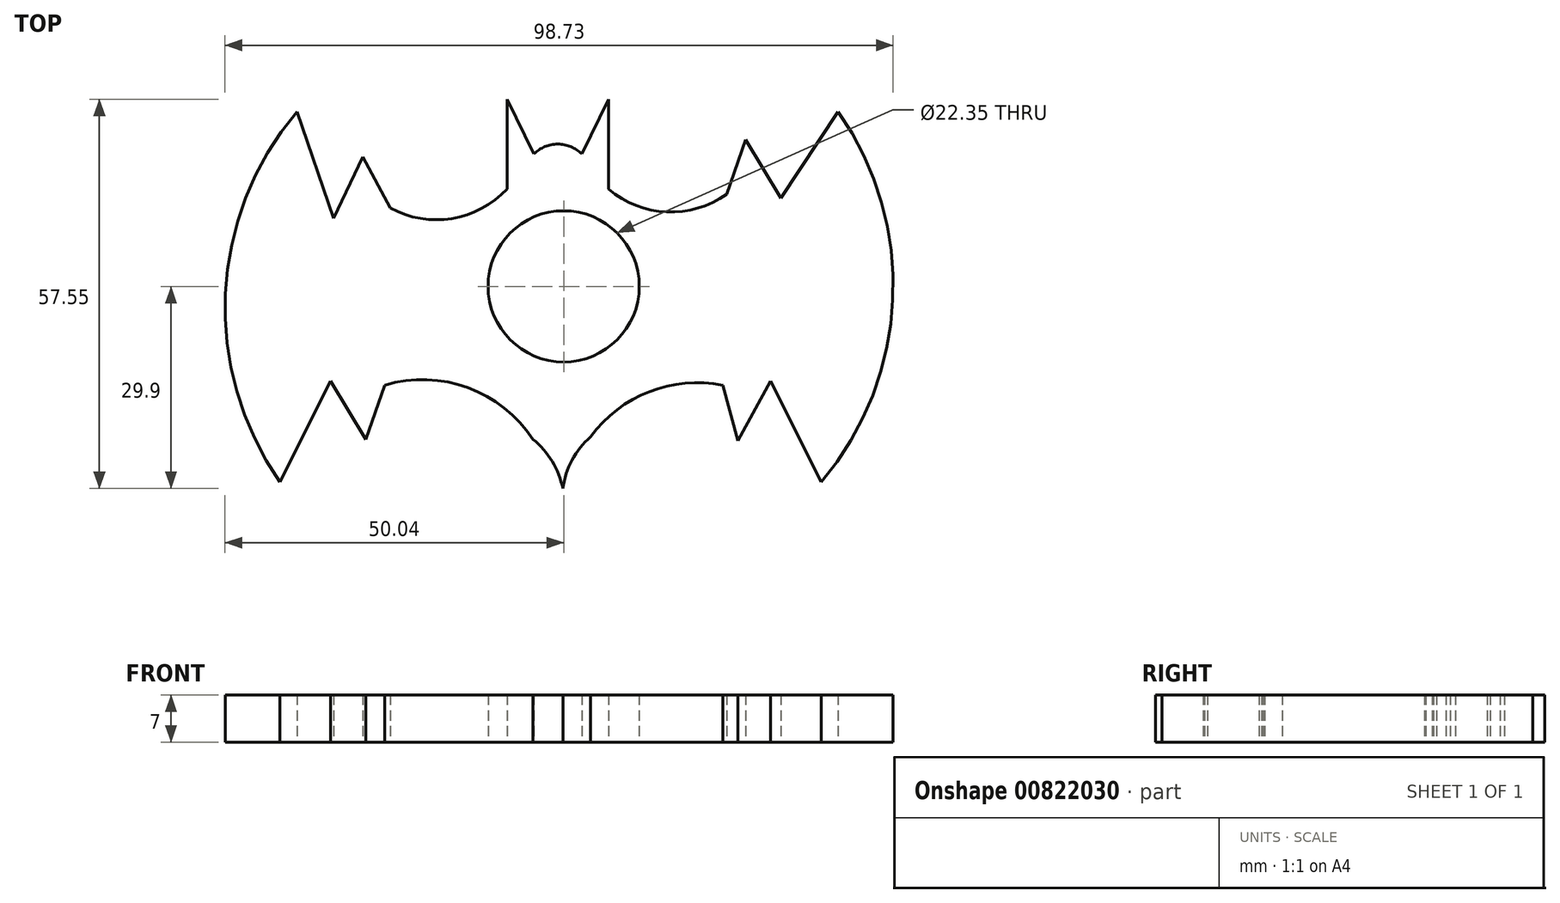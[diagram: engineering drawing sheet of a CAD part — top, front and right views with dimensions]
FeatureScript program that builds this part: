
annotation { "Feature Type Name" : "Feature", "Feature Type Description" : "" }
export const myFeature = defineFeature(function(context is Context, id is Id, definition is map)
    precondition{}
    {
        {
            var Q0;
            Q0=qCreatedBy(makeId("Top.planeOp"),FACE);
            var sketch = newSketch(context, id + "F0", { "sketchPlane" : qUnion([Q0])});
            skCircle(sketch, "E0", {"center": v(0, 0) * mm, "radius": 11.18 * mm});
            skCircle(sketch, "E1", {"center": v(0, 0) * mm, "radius": 12.7 * mm});
            skArc(sketch, "E2", {"start": v(-39.43, 25.83) * mm, "mid": v(-50, -1.12) * mm, "end": v(-41.92, -28.92) * mm});
            skArc(sketch, "E3.1.0", {"start": v(38.08, -28.92) * mm, "mid": v(48.64, -1.97) * mm, "end": v(40.57, 25.83) * mm});
            skPoint(sketch, "E3.center", {"position": v(-0.67, -1.55) * mm});
            skLineSegment(sketch, "E4", {"start": v(-41.92, -28.92) * mm, "end": v(-34.42, -14.02) * mm});
            skArc(sketch, "E5", {"start": v(-4.53, -22.63) * mm, "mid": v(-14.16, -14.98) * mm, "end": v(-26.46, -14.62) * mm});
            skLineSegment(sketch, "E6.1.0", {"start": v(40.57, 25.83) * mm, "end": v(32.07, 13.03) * mm});
            skLineSegment(sketch, "E6.1.1", {"start": v(32.07, 13.03) * mm, "end": v(26.9, 21.68) * mm});
            skLineSegment(sketch, "E6.1.2", {"start": v(26.9, 21.68) * mm, "end": v(24.1, 13.63) * mm});
            skLineSegment(sketch, "E7", {"start": v(38.08, -28.92) * mm, "end": v(30.58, -14.02) * mm});
            skLineSegment(sketch, "E8", {"start": v(30.58, -14.02) * mm, "end": v(25.74, -22.85) * mm});
            skLineSegment(sketch, "E9", {"start": v(25.74, -22.85) * mm, "end": v(23.54, -14.62) * mm});
            skArc(sketch, "E10.1.0", {"start": v(-25.65, 11.6) * mm, "mid": v(-16.53, 10.03) * mm, "end": v(-8.37, 14.4) * mm});
            skLineSegment(sketch, "E10.1.2", {"start": v(-29.67, 19.12) * mm, "end": v(-25.65, 11.6) * mm});
            skLineSegment(sketch, "E10.1.4", {"start": v(-34.03, 10.04) * mm, "end": v(-29.67, 19.12) * mm});
            skLineSegment(sketch, "E10.1.5", {"start": v(-39.43, 25.83) * mm, "end": v(-34.03, 10.04) * mm});
            skArc(sketch, "E11", {"start": v(0, -34.06) * mm, "mid": v(-0.76, -27.75) * mm, "end": v(-4.53, -22.63) * mm});
            skArc(sketch, "E12.1.0", {"start": v(6.63, 14.4) * mm, "mid": v(15.24, 11) * mm, "end": v(24.1, 13.63) * mm});
            skLineSegment(sketch, "E13", {"start": v(-8.37, 14.4) * mm, "end": v(-8.37, 27.65) * mm});
            skLineSegment(sketch, "E14", {"start": v(-8.37, 27.65) * mm, "end": v(-4.42, 19.56) * mm});
            skLineSegment(sketch, "E15", {"start": v(6.63, 14.4) * mm, "end": v(6.63, 27.65) * mm});
            skLineSegment(sketch, "E16", {"start": v(6.63, 27.65) * mm, "end": v(2.68, 19.56) * mm});
            skArc(sketch, "E17", {"start": v(2.68, 19.56) * mm, "mid": v(-0.87, 21.04) * mm, "end": v(-4.42, 19.56) * mm});
            skArc(sketch, "E18", {"start": v(23.54, -14.62) * mm, "mid": v(12.64, -15.57) * mm, "end": v(3.97, -22.24) * mm});
            skArc(sketch, "E19", {"start": v(3.97, -22.24) * mm, "mid": v(0.4, -27.62) * mm, "end": v(0, -34.06) * mm});
            skLineSegment(sketch, "E20.1.0", {"start": v(-34.42, -14.02) * mm, "end": v(-29.26, -22.67) * mm});
            skLineSegment(sketch, "E20.1.1", {"start": v(-29.26, -22.67) * mm, "end": v(-26.46, -14.62) * mm});
            skPoint(sketch, "E20.center", {"position": v(-1.18, -0.5) * mm});
            skSolve(sketch);
        }
        {
            var Q0;
            Q0=makeQuery(id+"F0.imprint","IMPRINT",FACE,{"disambiguationData":[TD([[makeQuery(id+"F0.imprint","IMPRINT",EDGE,{"derivedFrom":sQuery(id+"F0.wireOp",EDGE,"E0")}),-1.0]])]});
            var Q1;
            Q1=makeQuery(id+"F0.imprint","IMPRINT",FACE,{"disambiguationData":[TD([[makeQuery(id+"F0.imprint","IMPRINT",EDGE,{"derivedFrom":sQuery(id+"F0.wireOp",EDGE,"E1")}),-1.0]])]});
            extrude(context, id + "F1", {"entities" : qUnion([Q0, Q1]), "depth" : 7 * mm, "offsetDistance" : 25 * mm});
        }
    });
